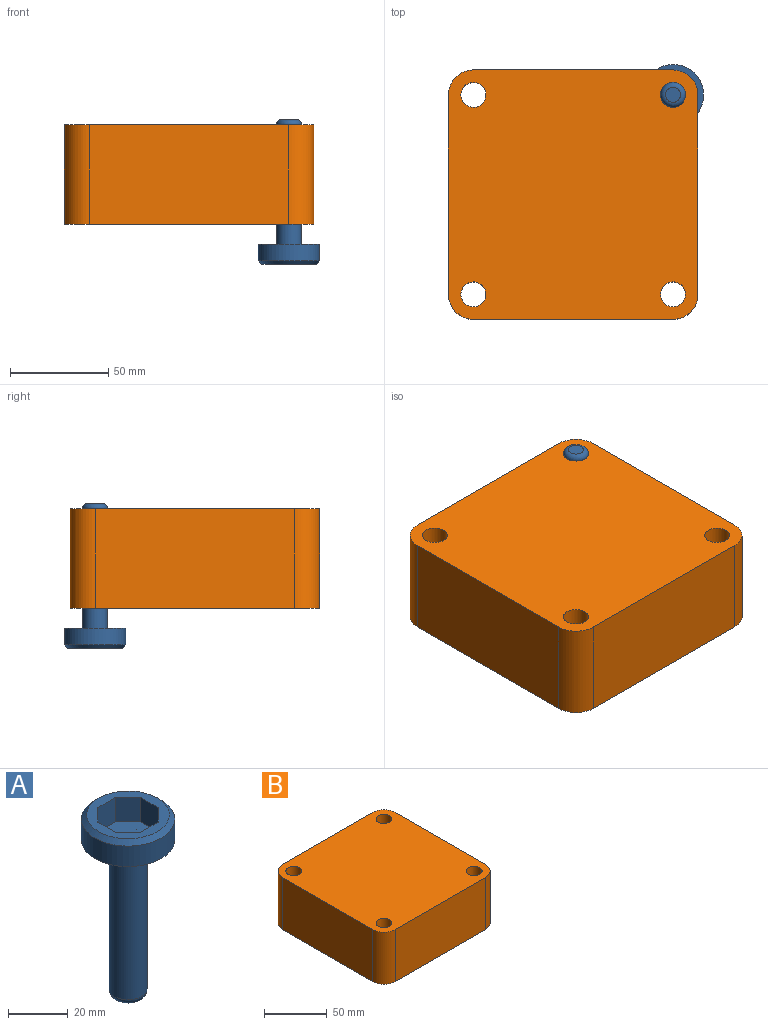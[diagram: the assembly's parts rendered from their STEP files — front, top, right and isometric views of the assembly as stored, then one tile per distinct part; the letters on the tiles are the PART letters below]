
ASSEMBLY  parts=2 mates=1
PART A: 16 faces, bbox 31.1x31.1x73.7 mm
  f0: cylinder r=6.35mm len=60.96mm, axis (0,0,-1), area 2432.2mm2, adj f4,f15
  f1: plane 7.62x7.62mm, normal (0,0,-1), area 45.6mm2, adj f15
  f2: cylinder r=15.57mm len=31.15mm, axis (0,0,-1), area 820.2mm2, adj f4,f5
  f3: plane 27.59x27.59mm, normal (0,0,1), area 261.1mm2, adj f5,f6,f7,f8,f9,f10,f11,f12
  f4: plane 31.15x31.15mm, normal (0,0,-1), area 635.2mm2, adj f0,f2
  f5: cone r=13.8mm half-angle=45deg, axis (0,0,-1), area 232mm2, adj f2,f3
  f6: plane 9.91x5.91mm, normal (-0.71,0.71,0), area 82.7mm2, adj f3,f7,f13,f14
  f7: plane 9.91x8.35mm, normal (-1,0,0), area 82.7mm2, adj f3,f6,f8,f14
  f8: plane 9.91x5.91mm, normal (-0.71,-0.71,0), area 82.7mm2, adj f3,f7,f9,f14
  f9: plane 9.91x8.35mm, normal (0,-1,0), area 82.7mm2, adj f3,f8,f10,f14
  f10: plane 9.91x5.91mm, normal (0.71,-0.71,0), area 82.7mm2, adj f3,f9,f11,f14
  f11: plane 9.91x8.35mm, normal (1,0,0), area 82.7mm2, adj f3,f10,f12,f14
  f12: plane 9.91x5.91mm, normal (0.71,0.71,0), area 82.7mm2, adj f3,f11,f13,f14
  f13: plane 9.91x8.35mm, normal (0,1,0), area 82.7mm2, adj f3,f6,f12,f14
  f14: plane 20.16x20.16mm, normal (0,0,1), area 336.8mm2, adj f6,f7,f8,f9,f10,f11,f12,f13
  f15: torus R=3.81mm, axis (0,0,1), area 136mm2, adj f0,f1
PART B: 14 faces, bbox 127x127x50.8 mm
  f0: plane 101.6x50.8mm, normal (1,0,0), area 5161.3mm2, adj f1,f11,f12,f13
  f1: cylinder r=12.7mm len=50.8mm, axis (0,0,-1), area 1013.4mm2, adj f0,f2,f12,f13
  f2: plane 101.6x50.8mm, normal (0,1,0), area 5161.3mm2, adj f1,f3,f12,f13
  f3: cylinder r=12.7mm len=50.8mm, axis (0,0,-1), area 1013.4mm2, adj f2,f4,f12,f13
  f4: plane 101.6x50.8mm, normal (-1,0,0), area 5161.3mm2, adj f3,f5,f12,f13
  f5: cylinder r=12.7mm len=50.8mm, axis (0,0,-1), area 1013.4mm2, adj f4,f6,f12,f13
  f6: plane 101.6x50.8mm, normal (0,-1,0), area 5161.3mm2, adj f5,f11,f12,f13
  f7: cylinder r=6.35mm len=50.8mm, axis (0,0,-1), area 2026.8mm2, adj f12,f13
  f8: cylinder r=6.35mm len=50.8mm, axis (0,0,-1), area 2026.8mm2, adj f12,f13
  f9: cylinder r=6.35mm len=50.8mm, axis (0,0,-1), area 2026.8mm2, adj f12,f13
  f10: cylinder r=6.35mm len=50.8mm, axis (0,0,-1), area 2026.8mm2, adj f12,f13
  f11: cylinder r=12.7mm len=50.8mm, axis (0,0,-1), area 1013.4mm2, adj f0,f6,f12,f13
  f12: plane 127x127mm, normal (0,0,1), area 15483.8mm2, adj f0,f1,f2,f3,f4,f5,f6,f7
  f13: plane 127x127mm, normal (0,0,-1), area 15483.8mm2, adj f0,f1,f2,f3,f4,f5,f6,f7
PLACE A rot(axis=(1,-0.09,0),180deg) t=(-58.11,124.34,53.34)mm
PLACE B at identity fixed
MATE revolute B.f1 <-> A.f0  axis (0,0,1) through (47.31,55.04,50.8)mm
